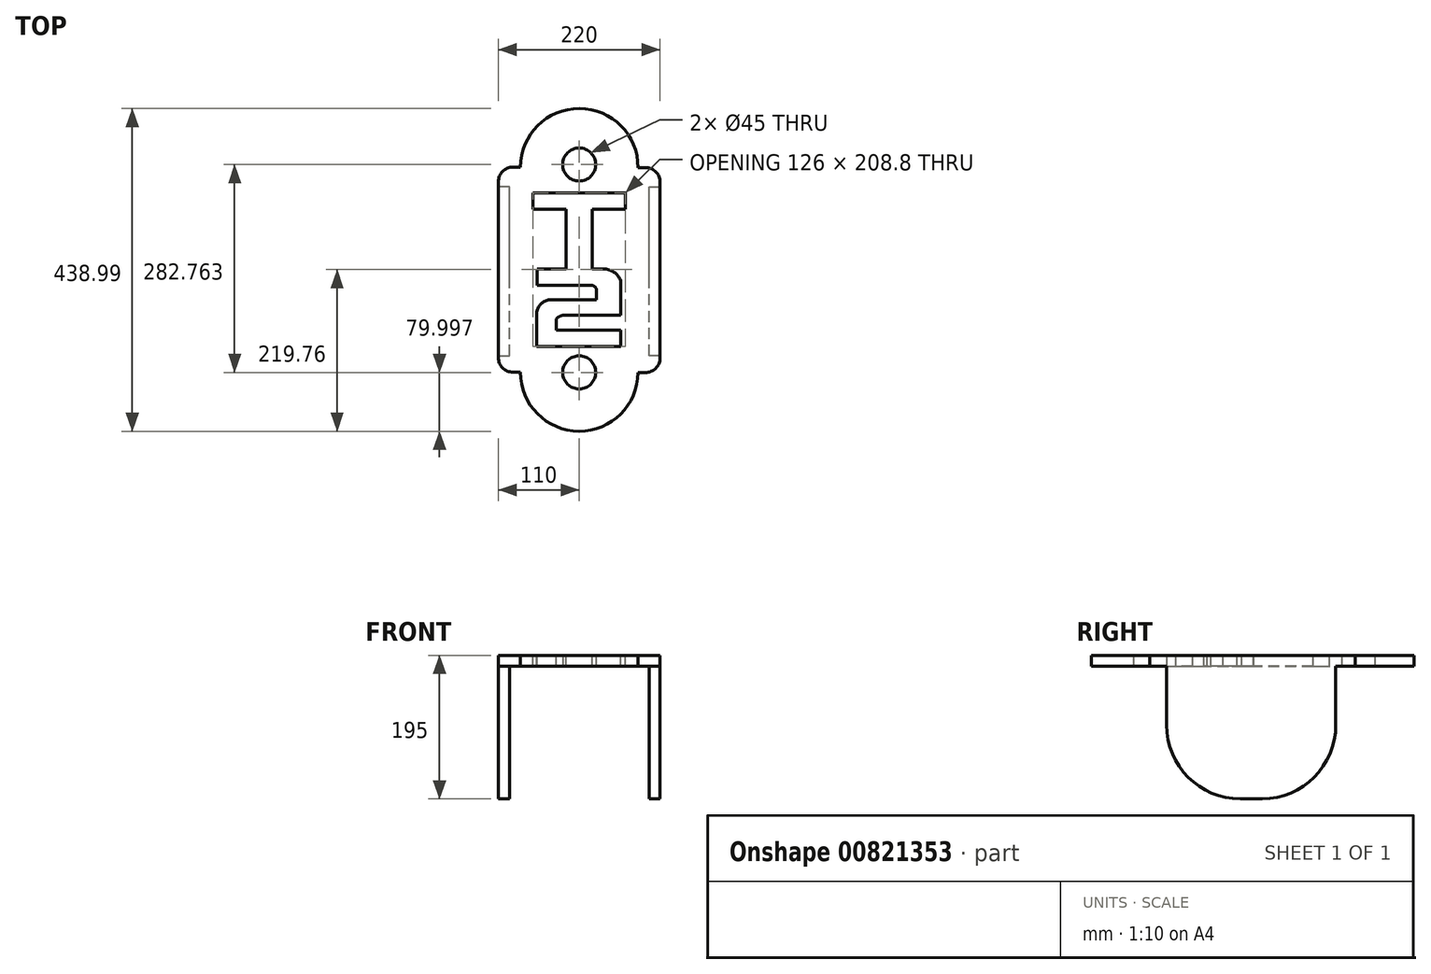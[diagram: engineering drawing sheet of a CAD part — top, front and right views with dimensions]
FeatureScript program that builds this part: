
annotation { "Feature Type Name" : "Feature", "Feature Type Description" : "" }
export const myFeature = defineFeature(function(context is Context, id is Id, definition is map)
    precondition{}
    {
        {
            var Q0;
            Q0=qCreatedBy(makeId("Top.planeOp"),FACE);
            var sketch = newSketch(context, id + "F0", { "sketchPlane" : qUnion([Q0])});
            skPoint(sketch, "E0.middle", {"position": v(0, 0) * mm});
            skPoint(sketch, "E1.center.orphan", {"position": v(0, 143) * mm});
            skPoint(sketch, "E2.center.orphan", {"position": v(0, -139.76) * mm});
            skCircle(sketch, "E3", {"center": v(0, 143) * mm, "radius": 22.5 * mm});
            skCircle(sketch, "E4", {"center": v(0, -139.76) * mm, "radius": 22.5 * mm});
            skLineSegment(sketch, "E5", {"start": v(70, 116) * mm, "end": v(-70, 116) * mm});
            skLineSegment(sketch, "E6", {"start": v(-70, 116) * mm, "end": v(-70, 91) * mm});
            skLineSegment(sketch, "E7", {"start": v(70, 91) * mm, "end": v(70, 116) * mm});
            skLineSegment(sketch, "E8", {"start": v(-70, 91) * mm, "end": v(-20, 91) * mm});
            skLineSegment(sketch, "E9", {"start": v(70, 91) * mm, "end": v(20, 91) * mm});
            skLineSegment(sketch, "E10", {"start": v(-20, 91) * mm, "end": v(-20, 1) * mm});
            skLineSegment(sketch, "E11", {"start": v(20, 91) * mm, "end": v(20, 1) * mm});
            skLineSegment(sketch, "E12", {"start": v(-63.35, 1.14) * mm, "end": v(-63.35, -23.86) * mm});
            skLineSegment(sketch, "E13", {"start": v(-63.35, -23.86) * mm, "end": v(19.65, -23.86) * mm});
            skLineSegment(sketch, "E14", {"start": v(62.78, -91.17) * mm, "end": v(-34.6, -91.17) * mm});
            skLineSegment(sketch, "E15", {"start": v(62.78, -16.67) * mm, "end": v(62.78, -68.95) * mm});
            skLineSegment(sketch, "E16", {"start": v(-22.83, -68.95) * mm, "end": v(62.78, -68.95) * mm});
            skLineSegment(sketch, "E17", {"start": v(-34.6, -91.17) * mm, "end": v(-34.6, -74.18) * mm});
            skLineSegment(sketch, "E18", {"start": v(62.78, -91.17) * mm, "end": v(62.78, -116) * mm});
            skLineSegment(sketch, "E19", {"start": v(62.78, -116) * mm, "end": v(-64, -116) * mm});
            skLineSegment(sketch, "E20", {"start": v(-64, -116) * mm, "end": v(-64, -63.72) * mm});
            skLineSegment(sketch, "E21", {"start": v(26.18, -31.7) * mm, "end": v(26.18, -45.42) * mm});
            skLineSegment(sketch, "E22", {"start": v(26.18, -45.42) * mm, "end": v(-42.43, -45.42) * mm});
            skArc(sketch, "E23", {"start": v(-42.43, -45.42) * mm, "mid": v(-56.58, -50.61) * mm, "end": v(-64, -63.72) * mm});
            skArc(sketch, "E24", {"start": v(62.78, -16.67) * mm, "mid": v(52.46, -3.73) * mm, "end": v(36.65, 1.14) * mm});
            skArc(sketch, "E25", {"start": v(26.18, -31.7) * mm, "mid": v(24.34, -26.6) * mm, "end": v(19.65, -23.86) * mm});
            skArc(sketch, "E26", {"start": v(-22.83, -68.95) * mm, "mid": v(-29.27, -70.31) * mm, "end": v(-34.6, -74.18) * mm});
            skPoint(sketch, "E27.startSnap0", {"position": v(0, 116) * mm});
            skLineSegment(sketch, "E28", {"start": v(110, -117.26) * mm, "end": v(95, -117.26) * mm});
            skLineSegment(sketch, "E29", {"start": v(95, -117.26) * mm, "end": v(95.08, 112.74) * mm});
            skPoint(sketch, "E30.endSnap0", {"position": v(-63.35, -11.36) * mm});
            skLineSegment(sketch, "E31", {"start": v(-20, 1) * mm, "end": v(-63.35, 1.14) * mm});
            skLineSegment(sketch, "E32", {"start": v(20, 1) * mm, "end": v(36.65, 1.14) * mm});
            skLineSegment(sketch, "E33", {"start": v(-110, -117.26) * mm, "end": v(-95, -117.26) * mm});
            skLineSegment(sketch, "E34", {"start": v(-95, -117.26) * mm, "end": v(-95, 112.74) * mm});
            skLineSegment(sketch, "E35", {"start": v(-110, 139.5) * mm, "end": v(-110, -139.49) * mm});
            skLineSegment(sketch, "E36", {"start": v(110, -140.04) * mm, "end": v(110, 138.95) * mm});
            skLineSegment(sketch, "E37", {"start": v(-95, 112.74) * mm, "end": v(-110, 112.74) * mm});
            skLineSegment(sketch, "E38", {"start": v(-110, 139.5) * mm, "end": v(-80, 139.5) * mm});
            skLineSegment(sketch, "E39", {"start": v(110, 138.95) * mm, "end": v(80, 138.95) * mm});
            skLineSegment(sketch, "E40", {"start": v(-110, -139.49) * mm, "end": v(-80, -139.49) * mm});
            skLineSegment(sketch, "E41", {"start": v(110, -140.04) * mm, "end": v(80, -140.04) * mm});
            skArc(sketch, "E42", {"start": v(-80, -139.49) * mm, "mid": v(-0.27, -219.76) * mm, "end": v(80, -140.04) * mm});
            skArc(sketch, "E43", {"start": v(80, 138.95) * mm, "mid": v(0.27, 219.22) * mm, "end": v(-80, 139.5) * mm});
            skLineSegment(sketch, "E44", {"start": v(95.08, 112.74) * mm, "end": v(110, 112.74) * mm});
            skSolve(sketch);
        }
        {
            var Q0;
            Q0 = qSketchRegion(id + "F0", true);
            var Q1;
            Q1=makeQuery(id+"F0.imprint","IMPRINT",FACE,{"disambiguationData":[TD([[makeQuery(id+"F0.imprint","IMPRINT",EDGE,{"derivedFrom":sQuery(id+"F0.wireOp",EDGE,"E5")}),1.0]])]});
            extrude(context, id + "F1", {"entities" : qUnion([Q0, Q1]), "depth" : 15 * mm, "offsetDistance" : 25 * mm});
        }
        {
            var Q0;
            {var subQ0=sQuery(id+"F0.wireOp",EDGE,"E33");Q0=makeQuery(id+"F0.imprint","IMPRINT",FACE,{"disambiguationData":[TD([[makeQuery(id+"F0.imprint","IMPRINT",EDGE,{"derivedFrom":subQ0}),1.0]])]});}
            var Q1;
            {var subQ0=sQuery(id+"F0.wireOp",EDGE,"E28");Q1=makeQuery(id+"F0.imprint","IMPRINT",FACE,{"disambiguationData":[TD([[makeQuery(id+"F0.imprint","IMPRINT",EDGE,{"derivedFrom":subQ0}),-1.0]])]});}
            extrude(context, id + "F2", {"entities" : qUnion([Q0, Q1]), "operationType" : NewBodyOperationType.ADD, "oppositeDirection" : true, "depth" : 180 * mm, "offsetDistance" : 25 * mm});
        }
        {
            var Q0;
            Q0=makeQuery(id+"F2.opExtrude","CAP_EDGE",EDGE,{"disambiguationData":[OSD([sQuery(id+"F0.wireOp",EDGE,"E28")])],"isStart":false});
            var Q1;
            Q1=makeQuery(id+"F2.opExtrude","CAP_EDGE",EDGE,{"disambiguationData":[OSD([sQuery(id+"F0.wireOp",EDGE,"ZKLfaSHL-Agax-IpBW-hiMC-YTN65XpPv0bT")])],"isStart":false});
            var Q2;
            Q2=makeQuery(id+"F2.opExtrude","CAP_EDGE",EDGE,{"disambiguationData":[OSD([sQuery(id+"F0.wireOp",EDGE,"DgvUId4f-ynFq-T6is-tCfe-JA8nvXV4FHGi")])],"isStart":false});
            var Q3;
            Q3=makeQuery(id+"F2.opExtrude","CAP_EDGE",EDGE,{"disambiguationData":[OSD([sQuery(id+"F0.wireOp",EDGE,"C2Jmj0KL-ToGo-FBOQ-GEjF-E8gLpnmCtN9i")])],"isStart":false});
            var Q4;
            Q4=makeQuery(id+"F2.opExtrude","CAP_EDGE",EDGE,{"disambiguationData":[OSD([sQuery(id+"F0.wireOp",EDGE,"uHRYx1Xk-GGiY-s3O2-EEeD-3TMG9aICvTUE")])],"isStart":false});
            var Q5;
            Q5=makeQuery(id+"F2.opExtrude","CAP_EDGE",EDGE,{"disambiguationData":[OSD([sQuery(id+"F0.wireOp",EDGE,"E33")])],"isStart":false});
            var Q6;
            Q6=makeQuery(id+"F2.opExtrude","CAP_EDGE",EDGE,{"disambiguationData":[OSD([sQuery(id+"F0.wireOp",EDGE,"E37")])],"isStart":false});
            var Q7;
            Q7=makeQuery(id+"F2.opExtrude","CAP_EDGE",EDGE,{"disambiguationData":[OSD([sQuery(id+"F0.wireOp",EDGE,"E44")])],"isStart":false});
            fillet(context, id + "F3", {"entities" : qUnion([Q0, Q1, Q2, Q3, Q4, Q5, Q6, Q7]), "radius" : 100 * mm, "tangentPropagation" : true, "allowEdgeOverflow" : false});
        }
        {
            var Q0;
            Q0=makeQuery(id+"F0.imprint","IMPRINT",FACE,{"disambiguationData":[TD([[makeQuery(id+"F0.imprint","IMPRINT",EDGE,{"derivedFrom":sQuery(id+"F0.wireOp",EDGE,"E5")}),1.0]])]});
            extrude(context, id + "F4", {"entities" : qUnion([Q0]), "depth" : 25 * mm, "offsetDistance" : 25 * mm});
        }
        {
            var Q0;
            Q0=makeQuery(id+"F4.opExtrude","SWEPT_BODY",BODY,{"disambiguationData":[OSD([sQuery(id+"F0.wireOp",EDGE,"E5"),sQuery(id+"F0.wireOp",EDGE,"E6"),sQuery(id+"F0.wireOp",EDGE,"E7"),sQuery(id+"F0.wireOp",EDGE,"E8"),sQuery(id+"F0.wireOp",EDGE,"E9"),sQuery(id+"F0.wireOp",EDGE,"E10"),sQuery(id+"F0.wireOp",EDGE,"E11"),sQuery(id+"F0.wireOp",EDGE,"E12"),sQuery(id+"F0.wireOp",EDGE,"E13"),sQuery(id+"F0.wireOp",EDGE,"E14"),sQuery(id+"F0.wireOp",EDGE,"E15"),sQuery(id+"F0.wireOp",EDGE,"E16"),sQuery(id+"F0.wireOp",EDGE,"E17"),sQuery(id+"F0.wireOp",EDGE,"E18"),sQuery(id+"F0.wireOp",EDGE,"E19"),sQuery(id+"F0.wireOp",EDGE,"E20"),sQuery(id+"F0.wireOp",EDGE,"E21"),sQuery(id+"F0.wireOp",EDGE,"E22"),sQuery(id+"F0.wireOp",EDGE,"E23"),sQuery(id+"F0.wireOp",EDGE,"E24"),sQuery(id+"F0.wireOp",EDGE,"E25"),sQuery(id+"F0.wireOp",EDGE,"E26"),sQuery(id+"F0.wireOp",EDGE,"E31"),sQuery(id+"F0.wireOp",EDGE,"E32")])]});
            var Q1;
            Q1=sQuery(id+"F0.wireOp",VERTEX,"E0.middle");
            transform(context, id + "F5", {"entities" : qUnion([Q0]), "transformType" : TransformType.SCALE_UNIFORMLY, "scale" : 0.9, "scalePoint" : qUnion([Q1]), "makeCopy" : false});
        }
        {
            var Q0;
            Q0=makeQuery(id+"F4.opExtrude","CAP_FACE",FACE,{"disambiguationData":[OSD([sQuery(id+"F0.wireOp",EDGE,"E5"),sQuery(id+"F0.wireOp",EDGE,"E6"),sQuery(id+"F0.wireOp",EDGE,"E7"),sQuery(id+"F0.wireOp",EDGE,"E8"),sQuery(id+"F0.wireOp",EDGE,"E9"),sQuery(id+"F0.wireOp",EDGE,"E10"),sQuery(id+"F0.wireOp",EDGE,"E11"),sQuery(id+"F0.wireOp",EDGE,"E12"),sQuery(id+"F0.wireOp",EDGE,"E13"),sQuery(id+"F0.wireOp",EDGE,"E14"),sQuery(id+"F0.wireOp",EDGE,"E15"),sQuery(id+"F0.wireOp",EDGE,"E16"),sQuery(id+"F0.wireOp",EDGE,"E17"),sQuery(id+"F0.wireOp",EDGE,"E18"),sQuery(id+"F0.wireOp",EDGE,"E19"),sQuery(id+"F0.wireOp",EDGE,"E20"),sQuery(id+"F0.wireOp",EDGE,"E21"),sQuery(id+"F0.wireOp",EDGE,"E22"),sQuery(id+"F0.wireOp",EDGE,"E23"),sQuery(id+"F0.wireOp",EDGE,"E24"),sQuery(id+"F0.wireOp",EDGE,"E25"),sQuery(id+"F0.wireOp",EDGE,"E26"),sQuery(id+"F0.wireOp",EDGE,"E31"),sQuery(id+"F0.wireOp",EDGE,"E32")])],"isStart":false});
            extrude(context, id + "F6", {"entities" : qUnion([Q0]), "operationType" : NewBodyOperationType.REMOVE, "oppositeDirection" : true, "depth" : 25 * mm, "offsetDistance" : 25 * mm});
        }
        {
            var Q0;
            Q0=makeQuery(id+"F1.opExtrude","SWEPT_EDGE",EDGE,{"disambiguationData":[OSD([sQuery(id+"F0.wireOp",EDGE,"E36"),sQuery(id+"F0.wireOp",EDGE,"E41")])]});
            var Q1;
            Q1=makeQuery(id+"F1.opExtrude","SWEPT_EDGE",EDGE,{"disambiguationData":[OSD([sQuery(id+"F0.wireOp",EDGE,"E35"),sQuery(id+"F0.wireOp",EDGE,"E40")])]});
            var Q2;
            Q2=makeQuery(id+"F1.opExtrude","SWEPT_EDGE",EDGE,{"disambiguationData":[OSD([sQuery(id+"F0.wireOp",EDGE,"E36"),sQuery(id+"F0.wireOp",EDGE,"E39")])]});
            var Q3;
            Q3=makeQuery(id+"F1.opExtrude","SWEPT_EDGE",EDGE,{"disambiguationData":[OSD([sQuery(id+"F0.wireOp",EDGE,"E35"),sQuery(id+"F0.wireOp",EDGE,"E38")])]});
            fillet(context, id + "F7", {"entities" : qUnion([Q0, Q1, Q2, Q3]), "radius" : 20 * mm, "tangentPropagation" : true, "allowEdgeOverflow" : false});
        }
    });
